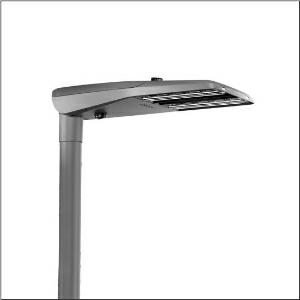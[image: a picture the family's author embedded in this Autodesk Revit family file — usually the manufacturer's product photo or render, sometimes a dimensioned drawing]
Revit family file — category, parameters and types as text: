
# Revit family: streetlight_sl_11_iq_midi___pc-l_5xc3e11y08me_a024
name_source: partatom
category: Lighting Fixtures
units: mm (PartAtom-declared; Revit-internal decimal feet)

## family parameters
Cut with Voids When Loaded = No
Host = Face
Light Source = No
Part Type = Normal
Room Calculation Point = No
Round Connector Dimension = Use Diameter
Shared = No

## types (1)
- --- (1 x LED, 9610 lm, 123.4 W, 1800K)
    Apparent Load = 123 VA
    CIE Flux Codes = 37 73 96 100 100
    Color Rendering = 70
    Color Temperature = 1800K
    Default Elevation = 1800 mm
    Description = Streetlight SL 11 iQ midi, mast luminaire, primary light control with 3 zone facetted reflector, of plastic, silver coated, highly specular, primary optical cover: cover, of PMMA, transparent, light distribution: PC-L, light emission: direct distribution, primary light characteristic: asymmetric, left, installation type: post-top, side-entry, lamps: LED, High Power LED, rated values: 9.610lm | 123,4W | 77,9lm/W (begin service life); end service life: 9.610lm | 130,9W; at 50% lumin. flux: 4.805lm | 54,1W | 88,8lm/W, colour temperature: 1800K, colour rendering: CRI > 70, light colour: 718, light setting 1 begin service life: 100% | 9.610lm | 123,4W | 77,9lm/W | 1.800K, light setting 1 end service life: 130,9W, further light settings possible, control: pre-setting: logarithmic dimming characteristic, Street-Remote, Auto-Match, Temp-Guard, Lumen-Switch, Night-Set, Smart-Wire, Light-Fading, Desk-Remote (wireless, voltage-free reading and setting of iQ features in the workshop via application-optimized NFC function/RFID function), optimised constant luminous flux control (CLO 2.0), with cable H07RN-F 5x 1.5mm², mains connection: 230..240V, AC, 50/60Hz, connection cable pre-assembled, cable length: 12,5m, luminaire housing, of diecast aluminium, powder-coated, Siteco® metallic grey (DB 702S), please order mast flange separately, inclination adjustable without tools: 0°, 5°, 10°, 15° (post-top) | 0°, -5°, -10°, -15° (side-entry), sealing non-destructively replaceable, multi-level sealing system, length: 780mm, width: 376mm, height: 118mm, mast flange for spigot size: 42mm (side-entry): 5XC10008XM4, 60/48mm (side-entry/post-top): 5XC10108XM2, 76/60mm (side-entry/post-top): 5XC10108XM1, equipment: Power, Smart Interface below and above, protection rating (complete): IP66, insulation class (complete): insulation class II (safety insulation), certification: CE, ENEC, ENEC+, VDE, UKCA, impact resistance: IK10, permissible operating ambient temperature for outdoor applications: -25..+50°C, standard-compliant lighting for roads and squares, Environmental Product Declaration (EPD) tested and certified by an independent institute, packaging unit: 1 piece

Light Distribution: PC-L
    Height = 118 mm
    Lamp = 1 x LED
    Lamp Light Flux = 9610 lm
    Lamp Power = 123.4 W
    Lamp count = 1
    Length = 780 mm
    Luminous efficacy = 78 lm/W
    Manufacturer = Siteco
    ModVariant = No
    Model = 5XC3E11Y08ME
    Number of Poles = 1
    OnlyDefault = Yes
    Power Factor = 1
    Product Name = Streetlight SL 11 iQ midi | PC-L
    Product group = mast luminaire | pylon top
    ProductGroupID = 6100
    Protection Class = Protection class II
    Protection Degree = IP 66
    RLX_Detail_Level = 1
    RLX_Emergency_Light_Flux = 0 lm
    RLX_Emergency_Type = 0
    RLX_Emergency_Type_DB = No
    RlxData = <blob elided: 73957 chars, md5=ef443137>
    Socket = socket
    Standby Power = 0 W
    System Light Flux = 9610 lm
    System Power = 123 W
    Type Comments = factory setting: luminous flux: 100 % | dim-lin: 254 | 553 mA
    Type Image = l_1004429.jpg
    URL = http://relux.com
    VarID = @adj_052539
    Voltage = 0 V
    Weight = 0.00 kg
    Width = 376 mm

## geometry (parser evidence)
native form markers: Blend x4, Sweep x11
no freeform markers — native parametric forms only
